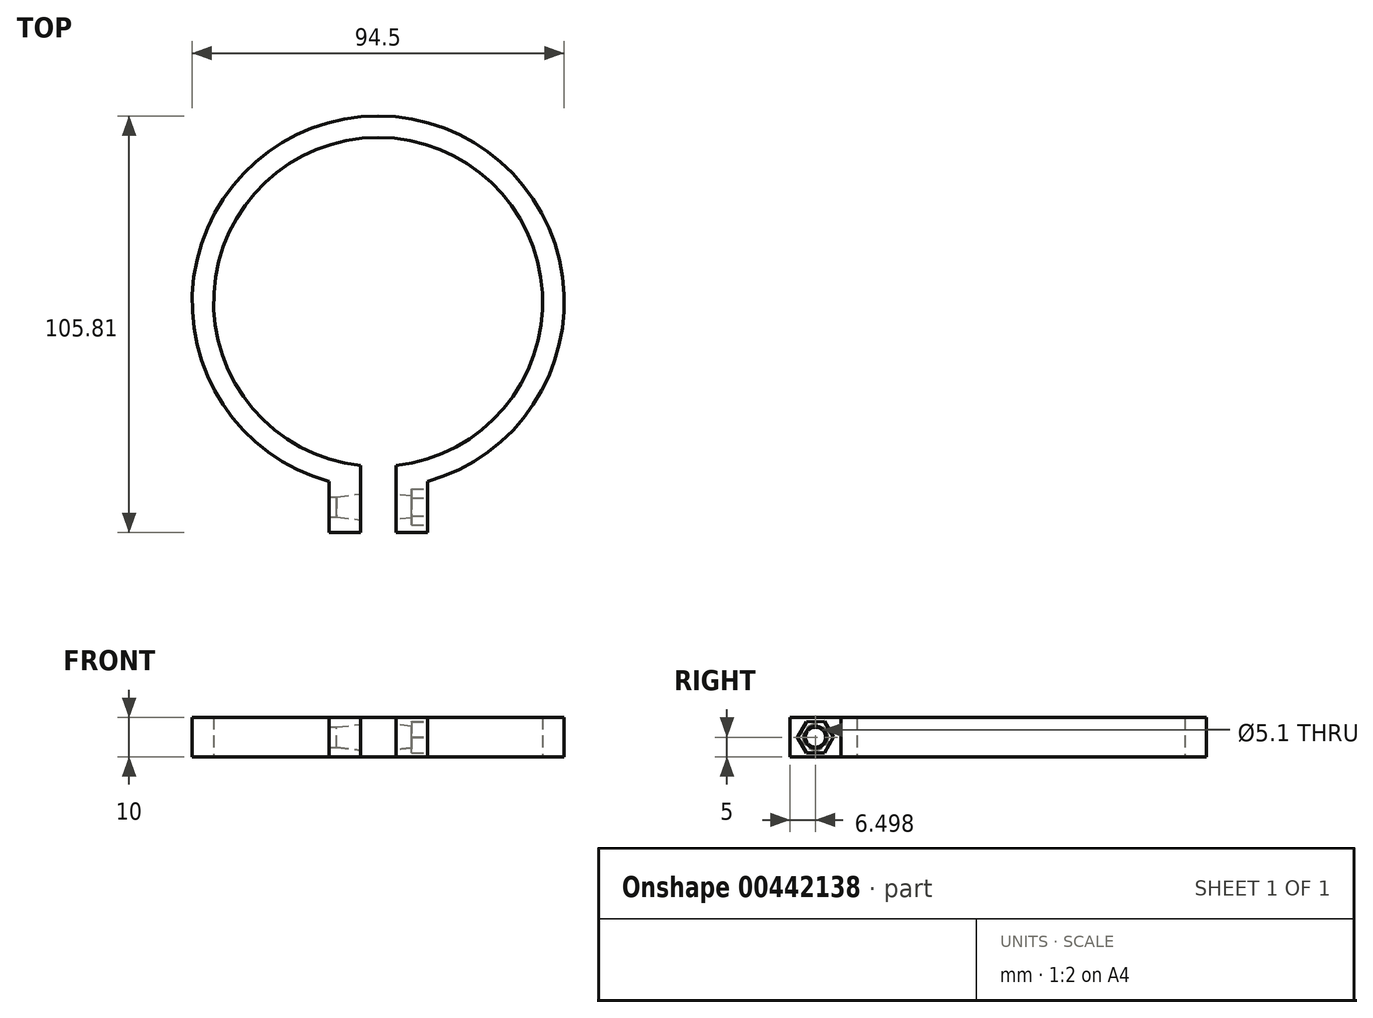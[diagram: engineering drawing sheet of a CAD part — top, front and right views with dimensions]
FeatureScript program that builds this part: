
annotation { "Feature Type Name" : "Feature", "Feature Type Description" : "" }
export const myFeature = defineFeature(function(context is Context, id is Id, definition is map)
    precondition{}
    {
        {
            var Q0;
            Q0=qCreatedBy(makeId("Top.planeOp"),FACE);
            var sketch = newSketch(context, id + "F0", { "sketchPlane" : qUnion([Q0])});
            skCircle(sketch, "E0", {"center": v(0, 0) * mm, "radius": 41.8 * mm});
            skCircle(sketch, "E1", {"center": v(0, 0) * mm, "radius": 47.25 * mm});
            skSolve(sketch);
        }
        {
            var Q0;
            Q0=makeQuery(id+"F0.imprint","IMPRINT",FACE,{"disambiguationData":[TD([[makeQuery(id+"F0.imprint","IMPRINT",EDGE,{"derivedFrom":sQuery(id+"F0.wireOp",EDGE,"E0")}),-1.0]])]});
            extrude(context, id + "F1", {"entities" : qUnion([Q0]), "depth" : 10 * mm});
        }
        {
            var Q0;
            Q0=qCreatedBy(makeId("Top.planeOp"),FACE);
            var sketch = newSketch(context, id + "F2", { "sketchPlane" : qUnion([Q0])});
            skLineSegment(sketch, "E2.bottom", {"start": v(0, -38.7) * mm, "end": v(4.5, -38.7) * mm});
            skLineSegment(sketch, "E2.top", {"start": v(0, -51.36) * mm, "end": v(4.5, -51.36) * mm});
            skLineSegment(sketch, "E2.left", {"start": v(0, -38.7) * mm, "end": v(0, -51.36) * mm});
            skLineSegment(sketch, "E2.right", {"start": v(4.5, -38.7) * mm, "end": v(4.5, -51.36) * mm});
            skLineSegment(sketch, "E3.MirrorCS", {"start": v(0, -51.36) * mm, "end": v(-4.5, -51.36) * mm});
            skLineSegment(sketch, "E4.MirrorCS", {"start": v(-4.5, -38.7) * mm, "end": v(-4.5, -51.36) * mm});
            skLineSegment(sketch, "E5.MirrorCS", {"start": v(0, -38.7) * mm, "end": v(-4.5, -38.7) * mm});
            skSolve(sketch);
        }
        {
            var Q0;
            Q0=makeQuery(id+"F2.imprint","IMPRINT",FACE,{"disambiguationData":[TD([[makeQuery(id+"F2.imprint","IMPRINT",EDGE,{"derivedFrom":sQuery(id+"F2.wireOp",EDGE,"E2.left")}),-1.0]])]});
            var Q1;
            Q1=makeQuery(id+"F2.imprint","IMPRINT",FACE,{"disambiguationData":[TD([[makeQuery(id+"F2.imprint","IMPRINT",EDGE,{"derivedFrom":sQuery(id+"F2.wireOp",EDGE,"E2.bottom")}),-1.0]])]});
            extrude(context, id + "F3", {"entities" : qUnion([Q0, Q1]), "operationType" : NewBodyOperationType.REMOVE, "depth" : 25 * mm});
        }
        {
            var Q0;
            Q0=qCreatedBy(makeId("Top.planeOp"),FACE);
            var sketch = newSketch(context, id + "F4", { "sketchPlane" : qUnion([Q0])});
            skLineSegment(sketch, "E6.bottom", {"start": v(-4.5, -41.56) * mm, "end": v(-12.5, -41.56) * mm});
            skLineSegment(sketch, "E6.top", {"start": v(-4.5, -58.56) * mm, "end": v(-12.5, -58.56) * mm});
            skLineSegment(sketch, "E6.left", {"start": v(-4.5, -41.56) * mm, "end": v(-4.5, -58.56) * mm});
            skLineSegment(sketch, "E6.right", {"start": v(-12.5, -41.56) * mm, "end": v(-12.5, -58.56) * mm});
            skLineSegment(sketch, "E7.MirrorCS", {"start": v(4.5, -58.56) * mm, "end": v(12.5, -58.56) * mm});
            skLineSegment(sketch, "E8.MirrorCS", {"start": v(12.5, -41.56) * mm, "end": v(12.5, -58.56) * mm});
            skLineSegment(sketch, "E9.MirrorCS", {"start": v(4.5, -41.56) * mm, "end": v(4.5, -58.56) * mm});
            skLineSegment(sketch, "E10.MirrorCS", {"start": v(4.5, -41.56) * mm, "end": v(12.5, -41.56) * mm});
            skSolve(sketch);
        }
        {
            var Q0;
            Q0=makeQuery(id+"F4.imprint","IMPRINT",FACE,{"disambiguationData":[TD([[makeQuery(id+"F4.imprint","IMPRINT",EDGE,{"derivedFrom":sQuery(id+"F4.wireOp",EDGE,"E7.MirrorCS")}),1.0]])]});
            var Q1;
            Q1=makeQuery(id+"F4.imprint","IMPRINT",FACE,{"disambiguationData":[TD([[makeQuery(id+"F4.imprint","IMPRINT",EDGE,{"derivedFrom":sQuery(id+"F4.wireOp",EDGE,"E6.bottom")}),1.0]])]});
            extrude(context, id + "F5", {"entities" : qUnion([Q0, Q1]), "operationType" : NewBodyOperationType.ADD, "depth" : 10 * mm});
        }
        {
            var Q0;
            Q0=makeQuery(id+"F5.opExtrude","SWEPT_FACE",FACE,{"disambiguationData":[OSD([sQuery(id+"F4.wireOp",EDGE,"E8.MirrorCS")])]});
            var sketch = newSketch(context, id + "F6", { "sketchPlane" : qUnion([Q0])});
            skLineSegment(sketch, "E11", {"start": v(-58.56, 5) * mm, "end": v(-45.57, 5) * mm, "construction": true});
            skLineSegment(sketch, "E12", {"start": v(-52.06, 10) * mm, "end": v(-52.06, 0) * mm, "construction": true});
            skCircle(sketch, "E13", {"center": v(-52.06, 5) * mm, "radius": 4.55 * mm});
            skCircle(sketch, "E14.cCircle", {"center": v(-52.06, 5) * mm, "radius": 4.55 * mm, "construction": true});
            skLineSegment(sketch, "E14.0", {"start": v(-49.77, 1.07) * mm, "end": v(-54.32, 1.05) * mm});
            skLineSegment(sketch, "E14.1", {"start": v(-54.32, 1.05) * mm, "end": v(-56.61, 4.98) * mm});
            skLineSegment(sketch, "E14.2", {"start": v(-56.61, 4.98) * mm, "end": v(-54.35, 8.93) * mm});
            skLineSegment(sketch, "E14.3", {"start": v(-54.35, 8.93) * mm, "end": v(-49.8, 8.95) * mm});
            skLineSegment(sketch, "E14.4", {"start": v(-49.8, 8.95) * mm, "end": v(-47.51, 5.02) * mm});
            skLineSegment(sketch, "E14.5", {"start": v(-47.51, 5.02) * mm, "end": v(-49.77, 1.07) * mm});
            skSolve(sketch);
        }
        {
            var Q0;
            Q0=makeQuery(id+"F6.imprint","IMPRINT",FACE,{"disambiguationData":[TD([[makeQuery(id+"F6.imprint","IMPRINT",EDGE,{"derivedFrom":sQuery(id+"F6.wireOp",EDGE,"E14.0")}),-1.0]])]});
            extrude(context, id + "F7", {"entities" : qUnion([Q0]), "operationType" : NewBodyOperationType.REMOVE, "oppositeDirection" : true, "depth" : 4 * mm});
        }
        {
            var Q0;
            Q0=makeQuery(id+"F7.boolean.opBoolean","COPY",FACE,{"derivedFrom":makeQuery(id+"F7.opExtrude","CAP_FACE",FACE,{"disambiguationData":[OSD([sQuery(id+"F6.wireOp",EDGE,"E14.0"),sQuery(id+"F6.wireOp",EDGE,"E14.1"),sQuery(id+"F6.wireOp",EDGE,"E14.2"),sQuery(id+"F6.wireOp",EDGE,"E14.3"),sQuery(id+"F6.wireOp",EDGE,"E14.4"),sQuery(id+"F6.wireOp",EDGE,"E14.5")])],"isStart":false})});
            var sketch = newSketch(context, id + "F8", { "sketchPlane" : qUnion([Q0])});
            skLineSegment(sketch, "E15", {"start": v(-47.51, 5.02) * mm, "end": v(-56.61, 4.98) * mm, "construction": true});
            skLineSegment(sketch, "E16", {"start": v(-56.61, 4.98) * mm, "end": v(-52.05, 1.06) * mm, "construction": true});
            skLineSegment(sketch, "E17", {"start": v(-52.05, 1.06) * mm, "end": v(-52.08, 8.95) * mm, "construction": true});
            skCircle(sketch, "E18", {"center": v(-52.06, 5) * mm, "radius": 2.55 * mm});
            skSolve(sketch);
        }
        {
            var Q0;
            Q0=makeQuery(id+"F8.imprint","IMPRINT",FACE,{"disambiguationData":[TD([[makeQuery(id+"F8.imprint","IMPRINT",EDGE,{"derivedFrom":sQuery(id+"F8.wireOp",EDGE,"E18")}),1.0]])]});
            extrude(context, id + "F9", {"entities" : qUnion([Q0]), "operationType" : NewBodyOperationType.REMOVE, "oppositeDirection" : true, "depth" : 25 * mm});
        }
        {
            var Q0;
            Q0=makeQuery(id+"F9.boolean.opBoolean","INTERSECT",EDGE,{"derivedFrom":[makeQuery(id+"F5.boolean.opBoolean","MERGE",FACE,{"derivedFrom":[makeQuery(id+"F3.boolean.opBoolean","COPY",FACE,{"derivedFrom":makeQuery(id+"F3.opExtrude","SWEPT_FACE",FACE,{"disambiguationData":[OSD([sQuery(id+"F2.wireOp",EDGE,"E4.MirrorCS")])]})}),makeQuery(id+"F5.opExtrude","SWEPT_FACE",FACE,{"disambiguationData":[OSD([sQuery(id+"F4.wireOp",EDGE,"E6.left")])]})]}),makeQuery(id+"F9.opExtrude","SWEPT_FACE",FACE,{"disambiguationData":[OSD([sQuery(id+"F8.wireOp",EDGE,"E18")])]})]});
            chamfer(context, id + "F10", {"entities" : qUnion([Q0]), "chamferType" : ChamferType.OFFSET_ANGLE, "width" : 6 * mm, "oppositeDirection" : false, "angle" : 7 * degree, "tangentPropagation" : true});
        }
        {
            var Q0;
            Q0=makeQuery(id+"F9.boolean.opBoolean","INTERSECT",EDGE,{"derivedFrom":[makeQuery(id+"F5.boolean.opBoolean","MERGE",FACE,{"derivedFrom":[makeQuery(id+"F3.boolean.opBoolean","COPY",FACE,{"derivedFrom":makeQuery(id+"F3.opExtrude","SWEPT_FACE",FACE,{"disambiguationData":[OSD([sQuery(id+"F2.wireOp",EDGE,"E2.right")])]})}),makeQuery(id+"F5.opExtrude","SWEPT_FACE",FACE,{"disambiguationData":[OSD([sQuery(id+"F4.wireOp",EDGE,"E9.MirrorCS")])]})]}),makeQuery(id+"F9.opExtrude","SWEPT_FACE",FACE,{"disambiguationData":[OSD([sQuery(id+"F8.wireOp",EDGE,"E18")])]})]});
            chamfer(context, id + "F11", {"entities" : qUnion([Q0]), "chamferType" : ChamferType.OFFSET_ANGLE, "width" : 6 * mm, "oppositeDirection" : true, "angle" : 6 * degree, "tangentPropagation" : true});
        }
    });
